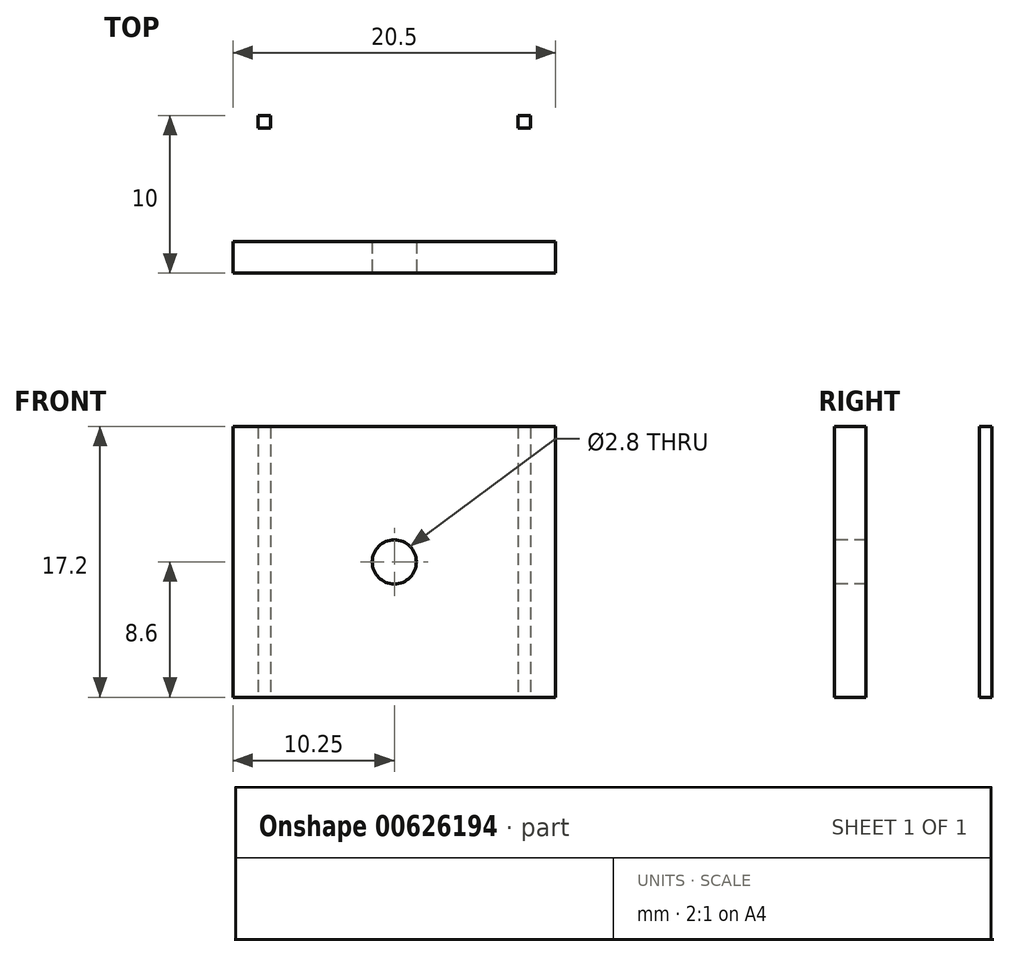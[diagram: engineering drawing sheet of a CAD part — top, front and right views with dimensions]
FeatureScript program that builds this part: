
annotation { "Feature Type Name" : "Feature", "Feature Type Description" : "" }
export const myFeature = defineFeature(function(context is Context, id is Id, definition is map)
    precondition{}
    {
        {
            var Q0;
            Q0=qCreatedBy(makeId("Top.planeOp"),FACE);
            var sketch = newSketch(context, id + "F0", { "sketchPlane" : qUnion([Q0])});
            skLineSegment(sketch, "E0.bottom", {"start": v(0, 0) * mm, "end": v(-10.25, 0) * mm});
            skLineSegment(sketch, "E0.top", {"start": v(0, 2) * mm, "end": v(-10.25, 2) * mm});
            skLineSegment(sketch, "E0.left", {"start": v(0, 0) * mm, "end": v(0, 2) * mm});
            skLineSegment(sketch, "E0.right", {"start": v(-10.25, 0) * mm, "end": v(-10.25, 2) * mm});
            skLineSegment(sketch, "E1.bottom", {"start": v(-10.25, 2) * mm, "end": v(-8.65, 2) * mm});
            skLineSegment(sketch, "E1.top", {"start": v(-10.25, 10) * mm, "end": v(-8.65, 10) * mm});
            skLineSegment(sketch, "E1.left", {"start": v(-10.25, 2) * mm, "end": v(-10.25, 10) * mm});
            skLineSegment(sketch, "E1.right", {"start": v(-8.65, 2) * mm, "end": v(-8.65, 10) * mm});
            skLineSegment(sketch, "E2.bottom", {"start": v(-8.65, 10) * mm, "end": v(-7.85, 10) * mm});
            skLineSegment(sketch, "E2.top", {"start": v(-8.65, 9.2) * mm, "end": v(-7.85, 9.2) * mm});
            skLineSegment(sketch, "E2.left", {"start": v(-8.65, 10) * mm, "end": v(-8.65, 9.2) * mm});
            skLineSegment(sketch, "E2.right", {"start": v(-7.85, 10) * mm, "end": v(-7.85, 9.2) * mm});
            skLineSegment(sketch, "E3.MirrorCS", {"start": v(8.65, 10) * mm, "end": v(7.85, 10) * mm});
            skLineSegment(sketch, "E4.MirrorCS", {"start": v(8.65, 9.2) * mm, "end": v(7.85, 9.2) * mm});
            skLineSegment(sketch, "E5.MirrorCS", {"start": v(8.65, 10) * mm, "end": v(8.65, 9.2) * mm});
            skLineSegment(sketch, "E6.MirrorCS", {"start": v(7.85, 10) * mm, "end": v(7.85, 9.2) * mm});
            skLineSegment(sketch, "E7.MirrorCS", {"start": v(0, 0) * mm, "end": v(10.25, 0) * mm});
            skLineSegment(sketch, "E8.MirrorCS", {"start": v(0, 2) * mm, "end": v(10.25, 2) * mm});
            skLineSegment(sketch, "E9.MirrorCS", {"start": v(10.25, 0) * mm, "end": v(10.25, 2) * mm});
            skLineSegment(sketch, "E10.MirrorCS", {"start": v(10.25, 2) * mm, "end": v(8.65, 2) * mm});
            skLineSegment(sketch, "E11.MirrorCS", {"start": v(10.25, 10) * mm, "end": v(8.65, 10) * mm});
            skLineSegment(sketch, "E12.MirrorCS", {"start": v(8.65, 2) * mm, "end": v(8.65, 10) * mm});
            skLineSegment(sketch, "E13.MirrorCS", {"start": v(10.25, 2) * mm, "end": v(10.25, 10) * mm});
            skSolve(sketch);
        }
        {
            var Q0;
            {var subQ0=sQuery(id+"F0.wireOp",EDGE,"E3.MirrorCS");Q0=makeQuery(id+"F0.imprint","IMPRINT",FACE,{"disambiguationData":[TD([[makeQuery(id+"F0.imprint","IMPRINT",EDGE,{"derivedFrom":subQ0}),1.0]])]});}
            var Q1;
            {var subQ3=sQuery(id+"F0.wireOp",EDGE,"E10.MirrorCS");Q1=makeQuery(id+"F0.imprint","IMPRINT",FACE,{"disambiguationData":[TD([[makeQuery(id+"F0.imprint","IMPRINT",EDGE,{"derivedFrom":subQ3}),-1.0]])]});}
            var Q2;
            Q2=makeQuery(id+"F0.imprint","IMPRINT",FACE,{"disambiguationData":[TD([[makeQuery(id+"F0.imprint","IMPRINT",EDGE,{"derivedFrom":sQuery(id+"F0.wireOp",EDGE,"E2.bottom")}),-1.0]])]});
            var Q3;
            Q3=makeQuery(id+"F0.imprint","IMPRINT",FACE,{"disambiguationData":[TD([[makeQuery(id+"F0.imprint","IMPRINT",EDGE,{"derivedFrom":sQuery(id+"F0.wireOp",EDGE,"E1.bottom")}),1.0]])]});
            var Q4;
            Q4=makeQuery(id+"F0.imprint","IMPRINT",FACE,{"disambiguationData":[TD([[makeQuery(id+"F0.imprint","IMPRINT",EDGE,{"derivedFrom":sQuery(id+"F0.wireOp",EDGE,"E0.bottom")}),-1.0]])]});
            var Q5;
            Q5=makeQuery(id+"F0.imprint","IMPRINT",FACE,{"disambiguationData":[TD([[makeQuery(id+"F0.imprint","IMPRINT",EDGE,{"derivedFrom":sQuery(id+"F0.wireOp",EDGE,"E7.MirrorCS")}),1.0]])]});
            extrude(context, id + "F1", {"entities" : qUnion([Q0, Q1, Q2, Q3, Q4, Q5]), "endBound" : BoundingType.SYMMETRIC, "depth" : 17.2 * mm, "offsetDistance" : 25 * mm});
        }
        {
            var Q0;
            Q0=makeQuery(id+"F1.opExtrude","SWEPT_FACE",FACE,{"disambiguationData":[OSD([sQuery(id+"F0.wireOp",EDGE,"E0.bottom"),sQuery(id+"F0.wireOp",EDGE,"E7.MirrorCS")])]});
            var sketch = newSketch(context, id + "F2", { "sketchPlane" : qUnion([Q0])});
            skCircle(sketch, "E14", {"center": v(0, 0) * mm, "radius": 1.4 * mm});
            skSolve(sketch);
        }
        {
            var Q0;
            Q0=makeQuery(id+"F2.imprint","IMPRINT",FACE,{"disambiguationData":[TD([[makeQuery(id+"F2.imprint","IMPRINT",EDGE,{"derivedFrom":sQuery(id+"F2.wireOp",EDGE,"E14")}),1.0]])]});
            extrude(context, id + "F3", {"entities" : qUnion([Q0]), "operationType" : NewBodyOperationType.REMOVE, "endBound" : BoundingType.UP_TO_NEXT, "oppositeDirection" : true, "depth" : 25 * mm, "offsetDistance" : 25 * mm});
        }
    });
